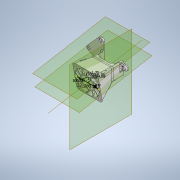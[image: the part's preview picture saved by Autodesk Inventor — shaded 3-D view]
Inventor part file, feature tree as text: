
AUTODESK INVENTOR PART (.ipt)
format: ipt  version: 2022 (Build 260153070, 153G)  size: 1,011,200 bytes
history: native  units: mm
features: sketch x16, extrude x14, reference x9, fillet x8, other x7, plane x6, loft x2, revolve x1, pattern_circular x1
ambient origin geometry x8: Origin, YZ Plane, XZ Plane, XY Plane, X Axis, Y Axis, Z Axis, Center Point
bodies: Solid1 (feature_tree)
feature tree (64):
  extrude  "Extrusion1"  Depth=2.5mm
  extrude  "Extrusion2"  Depth=5.0mm
  extrude  "Extrusion3"  Depth=2.0mm
  extrude  "Extrusion4"  Depth=0.25mm
  extrude  "Extrusion6"  Depth=14.45mm TaperAngle=0.0deg
  extrude  "Extrusion7"  TaperAngle=90.0deg  [1 undecoded]
  extrude  "Extrusion8"  Depth=5.0mm
  plane  "Work Plane2"
  fillet  "Fillet1"  Radius=1.0mm
  fillet  "Fillet2"  Radius=19.0mm
  fillet  "Fillet3"  Radius=2.0mm
  extrude  "Extrusion9"  Depth=2.5mm
  fillet  "Fillet4"  Radius=2.5mm
  sketch  "Sketch11"  dims[d34=2.0mm d35=38.0mm]
  plane  "Work Plane4"
  sketch  "Sketch12"  dims[d37=17.453293mm d38=20.0mm d39=6.981317mm]
  loft  "Loft2"
  loft  "Loft3"
  fillet  "Fillet5"  Radius=6.981317mm
  extrude  "Extrusion10"  Depth=80.0mm
  fillet  "Fillet6"  [1 undecoded]
  fillet  "Fillet7"  Radius=40.0mm
  extrude  "Extrusion11"  Depth=4.0mm
  fillet  "Fillet8"  Radius=2.8mm
  extrude  "Extrusion12"  Depth=20.0mm
  plane  "Work Plane5"
  extrude  "Extrusion13"  TaperAngle=0.0deg  [1 undecoded]
  plane  "Work Plane7"
  revolve  "Revolution1"  [1 undecoded]
  extrude  "Extrusion14"  Depth=10.0mm
  extrude  "Extrusion15"  Depth=10.0mm
  other  "Work Axis1"
  pattern_circular  "Circular Pattern1"  [2 undecoded]
  sketch  "Sketch1"  dims[d0=3.5mm d1=2.5mm]
  reference  "Reference1"
  reference  "Reference2"
  sketch  "Sketch2"  dims[d2=2.5mm d3=0.0mm d4=5.0mm]
  sketch  "Sketch3"  dims[d5=1.0mm d6=0.0mm d7=2.0mm]
  sketch  "Sketch4"  dims[d8=12.0mm d9=0.0mm d10=0.25mm]
  reference  "Reference3"
  reference  "Reference4"
  reference  "Reference5"
  reference  "Reference6"
  reference  "Reference7"
  sketch  "Sketch6"  dims[d11=3.0mm d12=0.0mm d17=14.45mm d18=0.0mm]
  sketch  "Sketch7"  dims[d19=90.0deg d21=90.0deg]
  reference  "Reference10"
  reference  "Reference11"
  sketch  "Sketch8"  dims[d22=3.5mm d23=0.0mm d24=5.0mm d25=1.0mm d26=0.0mm d27=19.0mm d28=2.0mm d29=2.0mm]
  sketch  "Sketch9"  dims[d30=2.0mm d31=2.5mm d32=2.5mm d33=0.0mm]
  plane  "Work Plane3"
  other  "Edges2"
  other  "Edges3"
  sketch  "Sketch13"  dims[d40=12.217305mm d41=80.0mm d42=90.0deg d43=40.0mm]
  sketch  "Sketch14"  dims[d44=40.0mm d45=4.0mm d46=2.8mm]
  sketch  "Sketch15"  dims[d49=38.0mm d50=20.0mm]
  plane  "Work Plane6"
  sketch  "Sketch18"  dims[d51=20.0mm d56=0.0mm d57=90.0deg]
  sketch  "Sketch19"  dims[d58=0.0mm d59=90.0deg]
  sketch  "Sketch20"  dims[d60=0.0mm d61=90.0deg d62=0.0mm d63=90.0deg d66=20.0mm d67=25.0mm d68=0.0mm d69=2.0mm d70=2.0mm d71=3.5mm d72=2.5mm d73=0.0mm d74=2.0mm d75=100.0mm d76=0.0mm d77=10.0mm d78=19.5mm d79=25.0mm d80=3.0mm d81=1.5mm d82=3.75mm d83=4.75mm d84=4.75mm d85=10.0mm d86=5.0mm d87=0.0mm d89=90.0deg d90=20.0mm d91=22.0mm d95=48.869219mm d96=10.0mm d97=17.453293mm d98=22.68928mm d99=22.68928mm d100=10.0mm d101=15.0mm d102=9.5mm d103=360.0deg d104=15.0deg d105=1.0mm d106=1.0mm d107=2.0mm d108=0.0mm d109=1.3mm d110=0.0mm d111=120.0mm d112=360.0deg d114=1.75mm d115=1.75mm d116=1.75mm d117=1.75mm]
  other  "<userpath> laptop\Desktop\Custom3dpFanDuct\REF_MODEL\ENDER 3 ASSEMBLY.iam"
  other  "ENDER 3 ASSEMBLY.iam"
  other  "BACKPLATE:1"
  other  "ENDER 3 HEATBLOCK:1"
note: 6 required parameter values undecoded (feature->parameter linkage not recoverable at this tier; creation-order binding heuristic only, values carry confidence <= 0.55)